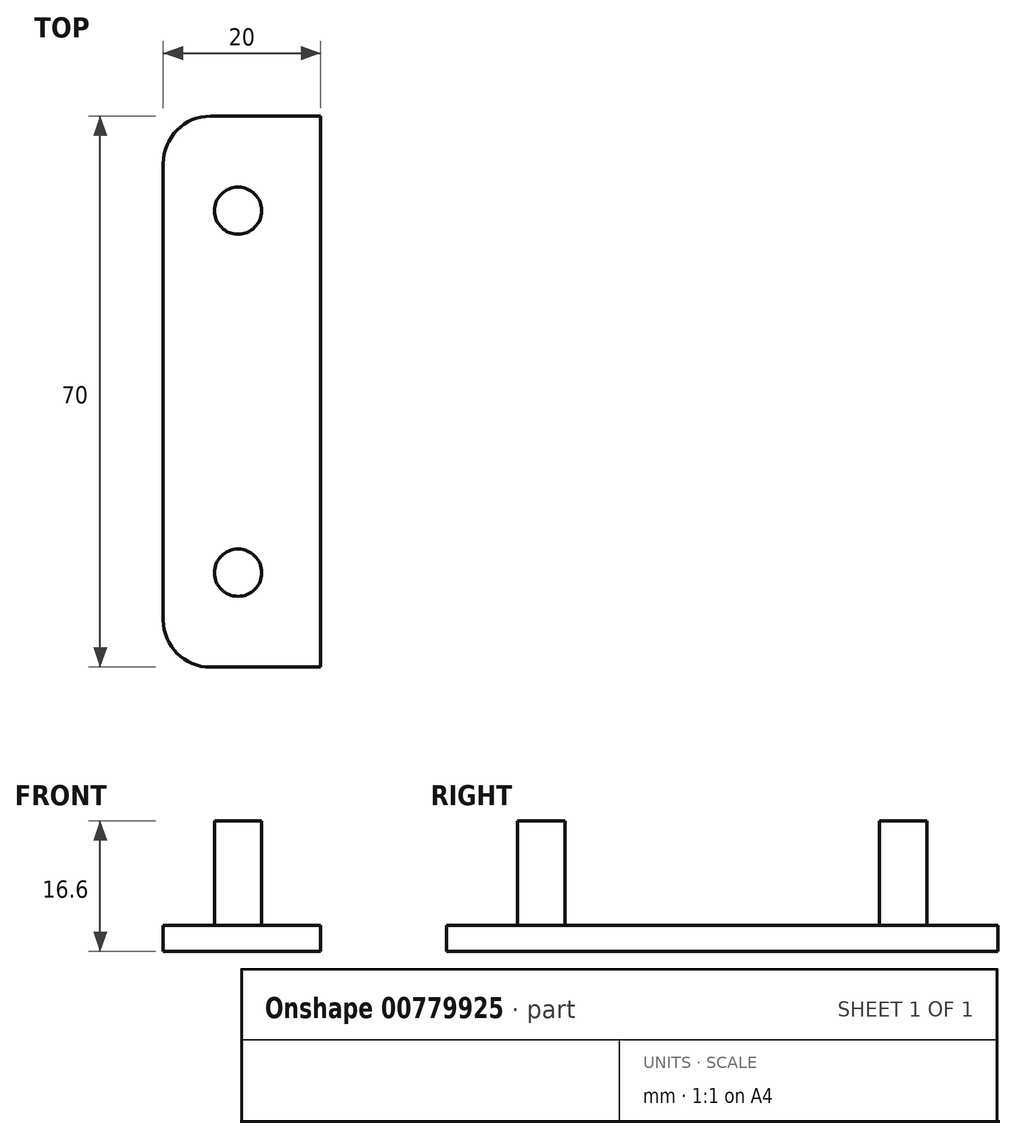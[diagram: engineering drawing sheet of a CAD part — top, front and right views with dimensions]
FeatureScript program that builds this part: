
annotation { "Feature Type Name" : "Feature", "Feature Type Description" : "" }
export const myFeature = defineFeature(function(context is Context, id is Id, definition is map)
    precondition{}
    {
        {
            var Q0;
            Q0=qCreatedBy(makeId("Front.planeOp"),FACE);
            var sketch = newSketch(context, id + "F0", { "sketchPlane" : qUnion([Q0])});
            skLineSegment(sketch, "E0", {"start": v(-12.79, 0) * mm, "end": v(7.21, 0) * mm});
            skLineSegment(sketch, "E1", {"start": v(7.21, 0) * mm, "end": v(7.21, 3.3) * mm});
            skLineSegment(sketch, "E2", {"start": v(7.21, 3.3) * mm, "end": v(-12.79, 3.3) * mm});
            skLineSegment(sketch, "E3", {"start": v(-12.79, 3.3) * mm, "end": v(-12.79, 0) * mm});
            skSolve(sketch);
        }
        {
            var Q0;
            Q0 = qSketchRegion(id + "F0", true);
            extrude(context, id + "F1", {"entities" : qUnion([Q0]), "depth" : 70 * mm, "offsetDistance" : 25 * mm});
        }
        {
            var Q0;
            Q0=makeQuery(id+"F1.opExtrude","SWEPT_FACE",FACE,{"disambiguationData":[OSD([sQuery(id+"F0.wireOp",EDGE,"E2")])]});
            var sketch = newSketch(context, id + "F2", { "sketchPlane" : qUnion([Q0])});
            skCircle(sketch, "E4", {"center": v(-3.29, -12) * mm, "radius": 3 * mm});
            skCircle(sketch, "E5", {"center": v(-3.29, -58) * mm, "radius": 3 * mm});
            skSolve(sketch);
        }
        {
            var Q0;
            Q0 = qSketchRegion(id + "F2", true);
            extrude(context, id + "F3", {"entities" : qUnion([Q0]), "operationType" : NewBodyOperationType.ADD, "depth" : 13.3 * mm, "offsetDistance" : 25 * mm});
        }
        {
            var Q0;
            Q0=makeQuery(id+"F1.opExtrude","CAP_EDGE",EDGE,{"disambiguationData":[OSD([sQuery(id+"F0.wireOp",EDGE,"E3")])],"isStart":true});
            var Q1;
            Q1=makeQuery(id+"F1.opExtrude","CAP_EDGE",EDGE,{"disambiguationData":[OSD([sQuery(id+"F0.wireOp",EDGE,"E3")])],"isStart":false});
            fillet(context, id + "F4", {"entities" : qUnion([Q0, Q1]), "radius" : 6 * mm, "tangentPropagation" : true, "allowEdgeOverflow" : false});
        }
    });
